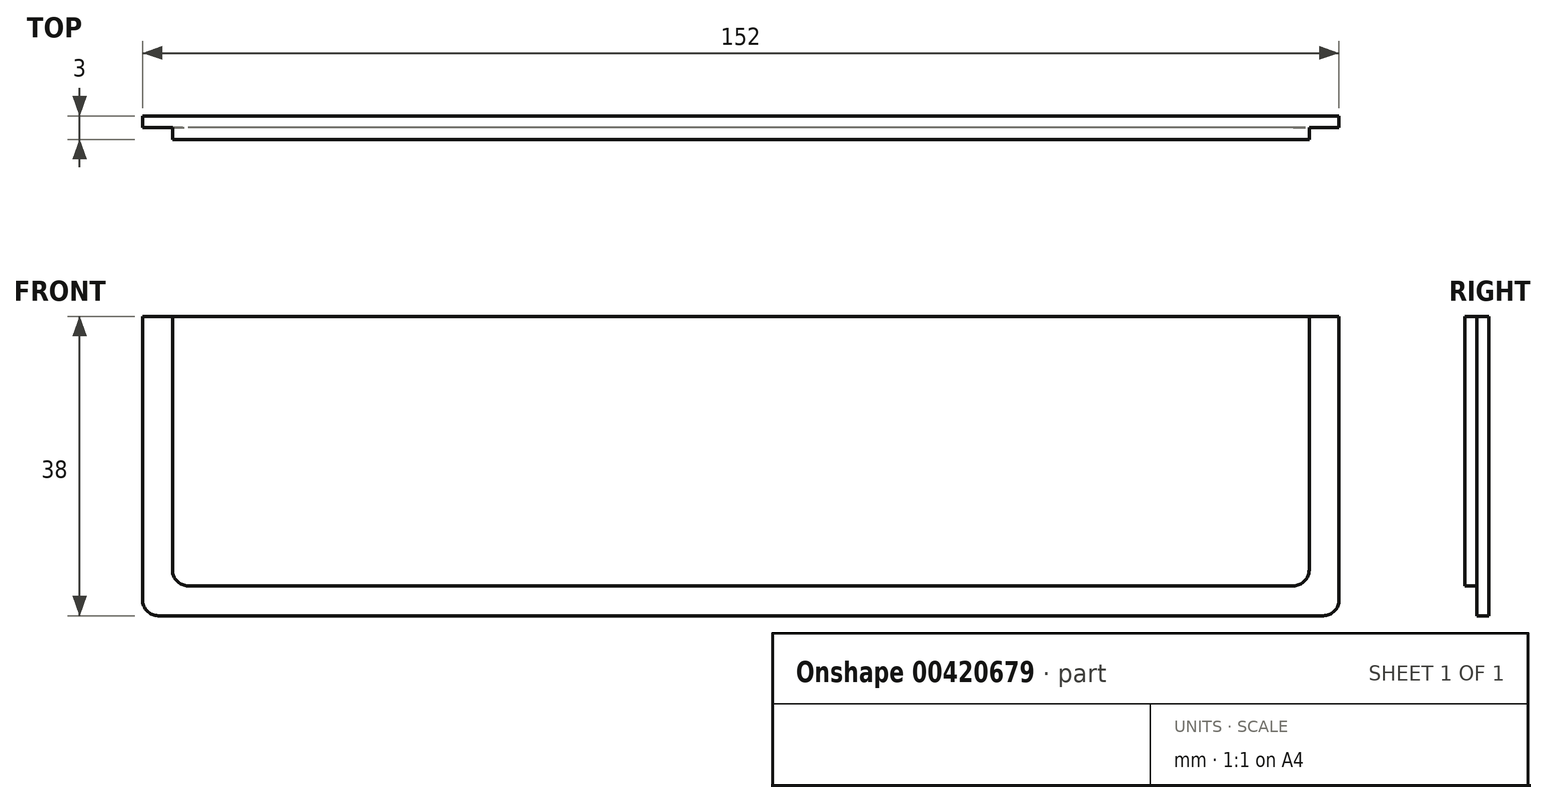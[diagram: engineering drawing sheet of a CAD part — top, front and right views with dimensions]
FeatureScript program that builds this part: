
annotation { "Feature Type Name" : "Feature", "Feature Type Description" : "" }
export const myFeature = defineFeature(function(context is Context, id is Id, definition is map)
    precondition{}
    {
        {
            var Q0;
            Q0=qCreatedBy(makeId("Front.planeOp"),FACE);
            var sketch = newSketch(context, id + "F0", { "sketchPlane" : qUnion([Q0])});
            skLineSegment(sketch, "E0.bottom", {"start": v(76, -19) * mm, "end": v(-76, -19) * mm});
            skLineSegment(sketch, "E0.top", {"start": v(76, 19) * mm, "end": v(-76, 19) * mm});
            skLineSegment(sketch, "E0.left", {"start": v(76, -19) * mm, "end": v(76, 19) * mm});
            skLineSegment(sketch, "E0.right", {"start": v(-76, -19) * mm, "end": v(-76, 19) * mm});
            skPoint(sketch, "E0.middle", {"position": v(0, 0) * mm});
            skSolve(sketch);
        }
        {
            var Q0;
            Q0=qSketchRegion(id+"F0",true);
            extrude(context, id + "F1", {"entities" : qUnion([Q0]), "depth" : 3 * mm});
        }
        {
            var Q0;
            Q0=makeQuery(id+"F1.opExtrude","CAP_FACE",FACE,{"disambiguationData":[OSD([sQuery(id+"F0.wireOp",EDGE,"E0.bottom"),sQuery(id+"F0.wireOp",EDGE,"E0.top"),sQuery(id+"F0.wireOp",EDGE,"E0.left"),sQuery(id+"F0.wireOp",EDGE,"E0.right")])],"isStart":false});
            var sketch = newSketch(context, id + "F2", { "sketchPlane" : qUnion([Q0])});
            skLineSegment(sketch, "E1", {"start": v(-76, 19) * mm, "end": v(-76, -19) * mm});
            skLineSegment(sketch, "E2", {"start": v(-76, -19) * mm, "end": v(76, -19) * mm});
            skLineSegment(sketch, "E3", {"start": v(76, -19) * mm, "end": v(76, 19) * mm});
            skLineSegment(sketch, "E4", {"start": v(76, 19) * mm, "end": v(72.2, 19) * mm});
            skLineSegment(sketch, "E5", {"start": v(72.2, 19) * mm, "end": v(72.2, -15.2) * mm});
            skLineSegment(sketch, "E6", {"start": v(72.2, -15.2) * mm, "end": v(-72.2, -15.2) * mm});
            skLineSegment(sketch, "E7", {"start": v(-72.2, -15.2) * mm, "end": v(-72.2, 19) * mm});
            skLineSegment(sketch, "E8", {"start": v(-72.2, 19) * mm, "end": v(-76, 19) * mm});
            skSolve(sketch);
        }
        {
            var Q0;
            Q0=qSketchRegion(id+"F2",true);
            extrude(context, id + "F3", {"entities" : qUnion([Q0]), "operationType" : NewBodyOperationType.REMOVE, "oppositeDirection" : true, "depth" : 1.5 * mm});
        }
        {
            var Q0;
            Q0=makeQuery(id+"F1.opExtrude","SWEPT_EDGE",EDGE,{"disambiguationData":[OSD([sQuery(id+"F0.wireOp",EDGE,"E0.bottom"),sQuery(id+"F0.wireOp",EDGE,"E0.left")])]});
            var Q1;
            Q1=makeQuery(id+"F3.boolean.opBoolean","COPY",EDGE,{"derivedFrom":makeQuery(id+"F3.opExtrude","SWEPT_EDGE",EDGE,{"disambiguationData":[OSD([sQuery(id+"F2.wireOp",EDGE,"E5"),sQuery(id+"F2.wireOp",EDGE,"E6")])]})});
            var Q2;
            Q2=makeQuery(id+"F1.opExtrude","SWEPT_EDGE",EDGE,{"disambiguationData":[OSD([sQuery(id+"F0.wireOp",EDGE,"E0.bottom"),sQuery(id+"F0.wireOp",EDGE,"E0.right")])]});
            var Q3;
            Q3=makeQuery(id+"F3.boolean.opBoolean","COPY",EDGE,{"derivedFrom":makeQuery(id+"F3.opExtrude","SWEPT_EDGE",EDGE,{"disambiguationData":[OSD([sQuery(id+"F2.wireOp",EDGE,"E6"),sQuery(id+"F2.wireOp",EDGE,"E7")])]})});
            fillet(context, id + "F4", {"entities" : qUnion([Q0, Q1, Q2, Q3]), "radius" : 2 * mm, "tangentPropagation" : true, "allowEdgeOverflow" : false});
        }
    });
